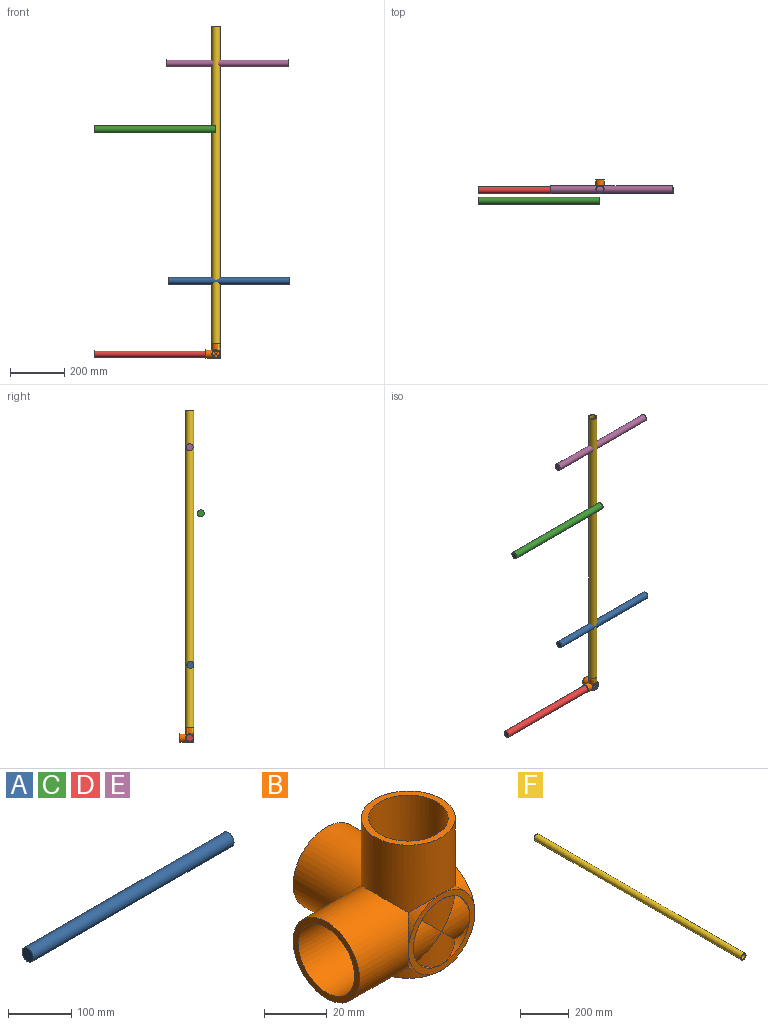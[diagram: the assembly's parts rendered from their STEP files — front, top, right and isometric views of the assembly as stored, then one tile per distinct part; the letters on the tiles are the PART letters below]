
ASSEMBLY  parts=6 mates=1
PART A: 3 faces, bbox 450x25.4x25.4 mm
  f0: cylinder r=12.7mm len=450mm, axis (1,0,0), area 35908.4mm2, adj f1,f2
  f1: plane 25.4x25.4mm, normal (-1,0,0), area 506.7mm2, adj f0
  f2: plane 25.4x25.4mm, normal (1,0,0), area 506.7mm2, adj f0
PART B: 108 faces, bbox 52x52x52 mm
  f0: cylinder r=12.7mm len=12.7mm, axis (0,-1,0), area 20.8mm2, adj f8,f56,f58
  f1: cylinder r=12.7mm len=12.7mm, axis (0,-1,0), area 20.8mm2, adj f8,f55,f57
  f2: cylinder r=12.7mm len=12.7mm, axis (0,-1,0), area 20.8mm2, adj f8,f55,f56
  f3: cylinder r=12.7mm len=12.7mm, axis (0,-1,0), area 20.8mm2, adj f8,f57,f58
  f4: cylinder r=15mm len=15mm, axis (0,-1,0), area 35.2mm2, adj f8,f18,f30
  f5: cylinder r=15mm len=15mm, axis (0,-1,0), area 35.2mm2, adj f8,f12,f29
  f6: cylinder r=15mm len=15mm, axis (0,-1,0), area 35.2mm2, adj f8,f25,f27
  f7: cylinder r=15mm len=15mm, axis (0,-1,0), area 35.2mm2, adj f8,f29,f30
  f8: plane 30x30mm, normal (0,-1,0), area 200.2mm2, adj f0,f1,f2,f3,f4,f5,f6,f7
  f9: cylinder r=15mm len=17.96mm, axis (-1,0,0), area 131.4mm2, adj f13,f35,f41,f59
  f10: cylinder r=15mm len=17.96mm, axis (-1,0,0), area 131.4mm2, adj f24,f42,f43
  f11: cylinder r=15mm len=15mm, axis (0,0,1), area 35.2mm2, adj f19,f26,f46
  f12: cylinder r=15mm len=15mm, axis (0,0,1), area 35.2mm2, adj f5,f26,f29
  f13: cylinder r=12.7mm len=12.7mm, axis (0,0,1), area 20.8mm2, adj f9,f26,f41
  f14: cylinder r=12.7mm len=12.7mm, axis (0,0,1), area 20.8mm2, adj f26,f31,f59
  f15: cylinder r=15mm len=17.96mm, axis (0,0,1), area 131.4mm2, adj f16,f38,f47,f48
  f16: cylinder r=12.7mm len=12.7mm, axis (-1,0,0), area 20.8mm2, adj f15,f28,f48
  f17: cylinder r=12.7mm len=12.7mm, axis (-1,0,0), area 20.8mm2, adj f28,f36,f47
  f18: cylinder r=15mm len=15mm, axis (-1,0,0), area 35.2mm2, adj f4,f28,f30
  f19: cylinder r=15mm len=15mm, axis (-1,0,0), area 35.2mm2, adj f11,f28,f46
  f20: cylinder r=15mm len=17.96mm, axis (0,0,1), area 131.4mm2, adj f21,f49,f50
  f21: cylinder r=12.7mm len=25.4mm, axis (-1,0,0), area 1838.5mm2, adj f20,f22,f40,f49,f50
  f22: plane 30x30mm, normal (-1,0,0), area 200.2mm2, adj f21,f29
  f23: plane 30x30mm, normal (0,0,1), area 200.2mm2, adj f24,f30
  f24: cylinder r=12.7mm len=25.4mm, axis (0,0,1), area 1838.5mm2, adj f10,f23,f32,f42,f43
  f25: cylinder r=15mm len=15mm, axis (0,0,1), area 35.2mm2, adj f6,f26,f27
  f26: plane 30x30mm, normal (0,0,-1), area 200.2mm2, adj f11,f12,f13,f14,f25,f33,f34,f35
  f27: cylinder r=15mm len=15mm, axis (-1,0,0), area 35.2mm2, adj f6,f25,f28
  f28: plane 30x30mm, normal (1,0,0), area 200.2mm2, adj f16,f17,f18,f19,f27,f37,f38,f39
  f29: cylinder r=15mm len=30mm, axis (-1,0,0), area 2214.4mm2, adj f5,f7,f12,f22,f30,f33,f46
  f30: cylinder r=15mm len=30mm, axis (0,0,1), area 2214.4mm2, adj f4,f7,f18,f23,f29,f39,f46
  f31: cylinder r=15mm len=17.96mm, axis (-1,0,0), area 131.4mm2, adj f14,f34,f41,f59
  f32: cylinder r=15mm len=17.96mm, axis (-1,0,0), area 131.4mm2, adj f24,f42,f43
  f33: cylinder r=15mm len=15mm, axis (0,0,1), area 35.2mm2, adj f26,f29,f46
  f34: cylinder r=12.7mm len=12.7mm, axis (0,0,1), area 20.8mm2, adj f26,f31,f41
  f35: cylinder r=12.7mm len=12.7mm, axis (0,0,1), area 20.8mm2, adj f9,f26,f59
  f36: cylinder r=15mm len=17.96mm, axis (0,0,1), area 131.4mm2, adj f17,f37,f47,f48
  f37: cylinder r=12.7mm len=12.7mm, axis (-1,0,0), area 20.8mm2, adj f28,f36,f48
  f38: cylinder r=12.7mm len=12.7mm, axis (-1,0,0), area 20.8mm2, adj f15,f28,f47
  f39: cylinder r=15mm len=15mm, axis (-1,0,0), area 35.2mm2, adj f28,f30,f46
  f40: cylinder r=15mm len=17.96mm, axis (0,0,1), area 131.4mm2, adj f21,f49,f50
  f41: cylinder r=15mm len=17.96mm, axis (0,-1,0), area 131.4mm2, adj f9,f13,f31,f34
  f42: cylinder r=15mm len=17.96mm, axis (0,-1,0), area 131.4mm2, adj f10,f24,f32
  f43: cylinder r=15mm len=17.96mm, axis (0,-1,0), area 131.4mm2, adj f10,f24,f32
  f44: cylinder r=12.7mm len=25.4mm, axis (0,-1,0), area 1838.5mm2, adj f45,f51,f52,f53,f54
  f45: plane 30x30mm, normal (0,1,0), area 200.2mm2, adj f44,f46
  f46: cylinder r=15mm len=30mm, axis (0,-1,0), area 2214.4mm2, adj f11,f19,f29,f30,f33,f39,f45
  f47: cylinder r=15mm len=17.96mm, axis (0,-1,0), area 131.4mm2, adj f15,f17,f36,f38
  f48: cylinder r=15mm len=17.96mm, axis (0,-1,0), area 131.4mm2, adj f15,f16,f36,f37
  f49: cylinder r=15mm len=17.96mm, axis (0,-1,0), area 131.4mm2, adj f20,f21,f40
  f50: cylinder r=15mm len=17.96mm, axis (0,-1,0), area 131.4mm2, adj f20,f21,f40
  f51: cylinder r=15mm len=17.96mm, axis (0,0,1), area 131.4mm2, adj f44,f52,f53
  f52: cylinder r=15mm len=17.96mm, axis (-1,0,0), area 131.4mm2, adj f44,f51,f54
  f53: cylinder r=15mm len=17.96mm, axis (-1,0,0), area 131.4mm2, adj f44,f51,f54
  f54: cylinder r=15mm len=17.96mm, axis (0,0,1), area 131.4mm2, adj f44,f52,f53
  f55: cylinder r=15mm len=17.96mm, axis (0,0,1), area 131.4mm2, adj f1,f2,f56,f57
  f56: cylinder r=15mm len=17.96mm, axis (-1,0,0), area 131.4mm2, adj f0,f2,f55,f58
  f57: cylinder r=15mm len=17.96mm, axis (-1,0,0), area 131.4mm2, adj f1,f3,f55,f58
  f58: cylinder r=15mm len=17.96mm, axis (0,0,1), area 131.4mm2, adj f0,f3,f56,f57
  f59: cylinder r=15mm len=17.96mm, axis (0,-1,0), area 131.4mm2, adj f9,f14,f31,f35
  f60: cylinder r=12.7mm len=13.97mm, axis (0,-1,0), area 45mm2, adj f61,f62
  f61: cylinder r=12.7mm len=13.97mm, axis (-1,0,0), area 45mm2, adj f60,f62
  f62: cylinder r=15mm len=13.97mm, axis (0,0,1), area 62mm2, adj f60,f61
  f63: cylinder r=12.7mm len=13.97mm, axis (0,-1,0), area 45mm2, adj f64,f65
  f64: cylinder r=15mm len=13.97mm, axis (0,0,1), area 62mm2, adj f63,f65
  f65: cylinder r=12.7mm len=13.97mm, axis (-1,0,0), area 45mm2, adj f63,f64
  f66: cylinder r=12.7mm len=13.97mm, axis (0,-1,0), area 45mm2, adj f67,f68
  f67: cylinder r=15mm len=13.97mm, axis (0,0,1), area 62mm2, adj f66,f68
  f68: cylinder r=12.7mm len=13.97mm, axis (-1,0,0), area 45mm2, adj f66,f67
  f69: cylinder r=12.7mm len=13.97mm, axis (0,-1,0), area 45mm2, adj f70,f71
  f70: cylinder r=15mm len=13.97mm, axis (0,0,1), area 62mm2, adj f69,f71
  f71: cylinder r=12.7mm len=13.97mm, axis (-1,0,0), area 45mm2, adj f69,f70
  f72: cylinder r=15mm len=13.97mm, axis (-1,0,0), area 62mm2, adj f73,f74
  f73: cylinder r=12.7mm len=13.97mm, axis (0,0,1), area 45mm2, adj f72,f74
  f74: cylinder r=12.7mm len=13.97mm, axis (0,-1,0), area 45mm2, adj f72,f73
  f75: cylinder r=15mm len=13.97mm, axis (-1,0,0), area 62mm2, adj f76,f77
  f76: cylinder r=12.7mm len=13.97mm, axis (0,0,1), area 45mm2, adj f75,f77
  f77: cylinder r=12.7mm len=13.97mm, axis (0,-1,0), area 45mm2, adj f75,f76
  f78: cylinder r=15mm len=13.97mm, axis (-1,0,0), area 62mm2, adj f79,f80
  f79: cylinder r=12.7mm len=13.97mm, axis (0,0,1), area 45mm2, adj f78,f80
  f80: cylinder r=12.7mm len=13.97mm, axis (0,-1,0), area 45mm2, adj f78,f79
  f81: cylinder r=15mm len=13.97mm, axis (-1,0,0), area 62mm2, adj f82,f83
  f82: cylinder r=12.7mm len=13.97mm, axis (0,0,1), area 45mm2, adj f81,f83
  f83: cylinder r=12.7mm len=13.97mm, axis (0,-1,0), area 45mm2, adj f81,f82
  f84: cylinder r=12.7mm len=13.97mm, axis (-1,0,0), area 45mm2, adj f85,f86
  f85: cylinder r=12.7mm len=13.97mm, axis (0,0,1), area 45mm2, adj f84,f86
  f86: cylinder r=15mm len=13.97mm, axis (0,-1,0), area 62mm2, adj f84,f85
  f87: cylinder r=15mm len=13.97mm, axis (0,-1,0), area 62mm2, adj f88,f89
  f88: cylinder r=12.7mm len=13.97mm, axis (0,0,1), area 45mm2, adj f87,f89
  f89: cylinder r=12.7mm len=13.97mm, axis (-1,0,0), area 45mm2, adj f87,f88
  f90: cylinder r=12.7mm len=13.97mm, axis (-1,0,0), area 45mm2, adj f91,f92
  f91: cylinder r=12.7mm len=13.97mm, axis (0,0,1), area 45mm2, adj f90,f92
  f92: cylinder r=15mm len=13.97mm, axis (0,-1,0), area 62mm2, adj f90,f91
  f93: cylinder r=12.7mm len=13.97mm, axis (-1,0,0), area 45mm2, adj f94,f95
  f94: cylinder r=12.7mm len=13.97mm, axis (0,0,1), area 45mm2, adj f93,f95
  f95: cylinder r=15mm len=13.97mm, axis (0,-1,0), area 62mm2, adj f93,f94
  f96: cylinder r=12.7mm len=17.96mm, axis (0,0,1), area 189mm2, adj f97,f99,f100,f107
  f97: cylinder r=12.7mm len=17.96mm, axis (-1,0,0), area 189mm2, adj f96,f98,f106,f107
  f98: cylinder r=12.7mm len=17.96mm, axis (0,0,1), area 189mm2, adj f97,f99,f101,f106
  f99: cylinder r=12.7mm len=17.96mm, axis (-1,0,0), area 189mm2, adj f96,f98,f100,f101
  f100: cylinder r=12.7mm len=17.96mm, axis (0,-1,0), area 189mm2, adj f96,f99,f102,f105
  f101: cylinder r=12.7mm len=17.96mm, axis (0,-1,0), area 189mm2, adj f98,f99,f102,f103
  f102: cylinder r=12.7mm len=17.96mm, axis (-1,0,0), area 189mm2, adj f100,f101,f103,f105
  f103: cylinder r=12.7mm len=17.96mm, axis (0,0,1), area 189mm2, adj f101,f102,f104,f106
  f104: cylinder r=12.7mm len=17.96mm, axis (-1,0,0), area 189mm2, adj f103,f105,f106,f107
  f105: cylinder r=12.7mm len=17.96mm, axis (0,0,1), area 189mm2, adj f100,f102,f104,f107
  f106: cylinder r=12.7mm len=17.96mm, axis (0,-1,0), area 189mm2, adj f97,f98,f103,f104
  f107: cylinder r=12.7mm len=17.96mm, axis (0,-1,0), area 189mm2, adj f96,f97,f104,f105
PART C: same geometry as A
PART D: same geometry as A
PART E: same geometry as A
PART F: 4 faces, bbox 30x1200x30 mm
  f0: cylinder r=12.7mm len=1200mm, axis (0,-1,0), area 95755.7mm2, adj f2,f3
  f1: cylinder r=15mm len=1200mm, axis (0,-1,0), area 113097.3mm2, adj f2,f3
  f2: plane 30x30mm, normal (0,1,0), area 200.2mm2, adj f0,f1
  f3: plane 30x30mm, normal (0,-1,0), area 200.2mm2, adj f0,f1
PLACE A rot(axis=(1,0,0),0.6deg) t=(273.12,-2.58,269.57)mm
PLACE B at identity
PLACE C rot(axis=(-1,0,0),4.5deg) t=(0,-41.18,828.99)mm
PLACE D at identity
PLACE E t=(267.48,0,1073.07)mm
PLACE F rot(axis=(1,0,0),90deg) t=(0,0,10.45)mm
MATE fastened F.f1 <-> B.f11  axis (0,0,-1) through (0,0,10.45)mm
